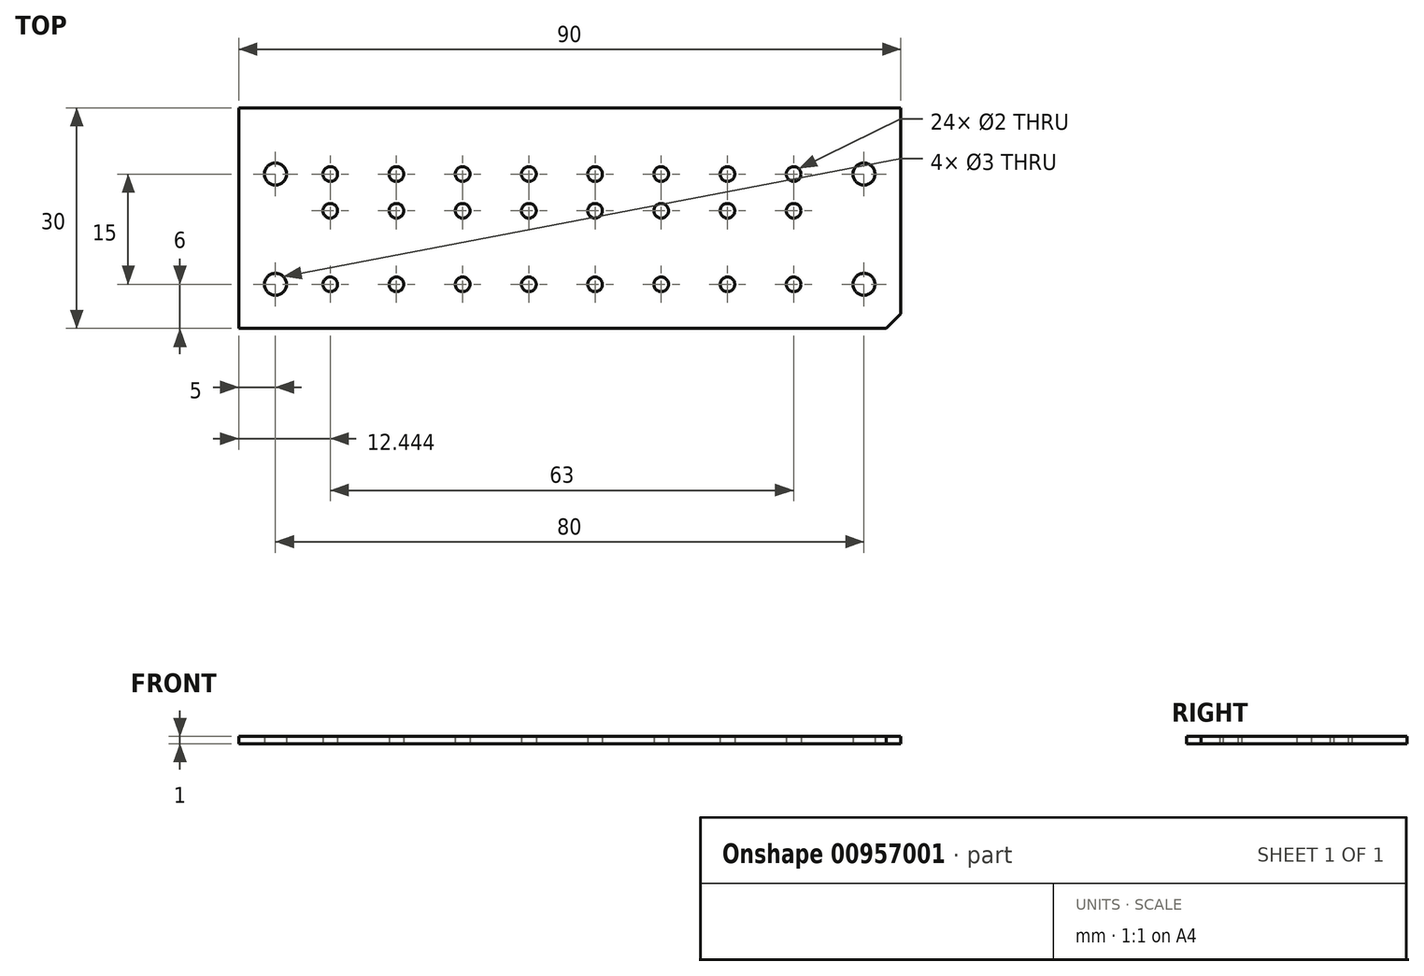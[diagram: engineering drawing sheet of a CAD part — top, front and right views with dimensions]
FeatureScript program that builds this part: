
annotation { "Feature Type Name" : "Feature", "Feature Type Description" : "" }
export const myFeature = defineFeature(function(context is Context, id is Id, definition is map)
    precondition{}
    {
        {
            var Q0;
            Q0=qCreatedBy(makeId("Top.planeOp"),FACE);
            var sketch = newSketch(context, id + "F0", { "sketchPlane" : qUnion([Q0])});
            skLineSegment(sketch, "E0.bottom", {"start": v(0, 0) * mm, "end": v(90, 0) * mm});
            skLineSegment(sketch, "E0.top", {"start": v(0, 30) * mm, "end": v(90, 30) * mm});
            skLineSegment(sketch, "E0.left", {"start": v(0, 0) * mm, "end": v(0, 30) * mm});
            skLineSegment(sketch, "E0.right", {"start": v(90, 0) * mm, "end": v(90, 30) * mm});
            skSolve(sketch);
        }
        {
            var Q0;
            Q0 = qSketchRegion(id + "F0", true);
            extrude(context, id + "F1", {"entities" : qUnion([Q0]), "depth" : 1 * mm, "offsetDistance" : 25 * mm});
        }
        {
            var Q0;
            Q0=qCreatedBy(makeId("Top.planeOp"),FACE);
            var sketch = newSketch(context, id + "F2", { "sketchPlane" : qUnion([Q0])});
            skCircle(sketch, "E1", {"center": v(12.44, 6) * mm, "radius": 1 * mm});
            skCircle(sketch, "E2", {"center": v(12.44, 21) * mm, "radius": 1 * mm});
            skCircle(sketch, "E3", {"center": v(12.44, 16) * mm, "radius": 1 * mm});
            skCircle(sketch, "E4.1.0.0", {"center": v(21.44, 21) * mm, "radius": 1 * mm});
            skCircle(sketch, "E4.1.0.1", {"center": v(21.44, 16) * mm, "radius": 1 * mm});
            skCircle(sketch, "E4.1.0.2", {"center": v(21.44, 6) * mm, "radius": 1 * mm});
            skCircle(sketch, "E4.2.0.0", {"center": v(30.44, 21) * mm, "radius": 1 * mm});
            skCircle(sketch, "E4.2.0.1", {"center": v(30.44, 16) * mm, "radius": 1 * mm});
            skCircle(sketch, "E4.2.0.2", {"center": v(30.44, 6) * mm, "radius": 1 * mm});
            skCircle(sketch, "E4.3.0.0", {"center": v(39.44, 21) * mm, "radius": 1 * mm});
            skCircle(sketch, "E4.3.0.1", {"center": v(39.44, 16) * mm, "radius": 1 * mm});
            skCircle(sketch, "E4.3.0.2", {"center": v(39.44, 6) * mm, "radius": 1 * mm});
            skCircle(sketch, "E4.4.0.0", {"center": v(48.44, 21) * mm, "radius": 1 * mm});
            skCircle(sketch, "E4.4.0.1", {"center": v(48.44, 16) * mm, "radius": 1 * mm});
            skCircle(sketch, "E4.4.0.2", {"center": v(48.44, 6) * mm, "radius": 1 * mm});
            skCircle(sketch, "E4.5.0.0", {"center": v(57.44, 21) * mm, "radius": 1 * mm});
            skCircle(sketch, "E4.5.0.1", {"center": v(57.44, 16) * mm, "radius": 1 * mm});
            skCircle(sketch, "E4.5.0.2", {"center": v(57.44, 6) * mm, "radius": 1 * mm});
            skCircle(sketch, "E4.6.0.0", {"center": v(66.44, 21) * mm, "radius": 1 * mm});
            skCircle(sketch, "E4.6.0.1", {"center": v(66.44, 16) * mm, "radius": 1 * mm});
            skCircle(sketch, "E4.6.0.2", {"center": v(66.44, 6) * mm, "radius": 1 * mm});
            skCircle(sketch, "E4.7.0.0", {"center": v(75.44, 21) * mm, "radius": 1 * mm});
            skCircle(sketch, "E4.7.0.1", {"center": v(75.44, 16) * mm, "radius": 1 * mm});
            skCircle(sketch, "E4.7.0.2", {"center": v(75.44, 6) * mm, "radius": 1 * mm});
            skLineSegment(sketch, "E4.direction1", {"start": v(12.44, 21) * mm, "end": v(21.44, 21) * mm, "construction": true});
            skSolve(sketch);
        }
        {
            var Q0;
            Q0 = qSketchRegion(id + "F2", true);
            var Q1;
            Q1=makeQuery(id+"F1.opExtrude","CAP_FACE",FACE,{"disambiguationData":[OSD([sQuery(id+"F0.wireOp",EDGE,"E0.bottom"),sQuery(id+"F0.wireOp",EDGE,"E0.top"),sQuery(id+"F0.wireOp",EDGE,"E0.left"),sQuery(id+"F0.wireOp",EDGE,"E0.right")])],"isStart":false});
            extrude(context, id + "F3", {"entities" : qUnion([Q0]), "operationType" : NewBodyOperationType.REMOVE, "endBound" : BoundingType.UP_TO_SURFACE, "depth" : 25 * mm, "endBoundEntityFace" : qUnion([Q1]), "offsetDistance" : 25 * mm});
        }
        {
            var Q0;
            Q0=makeQuery(id+"F1.opExtrude","SWEPT_EDGE",EDGE,{"disambiguationData":[OSD([sQuery(id+"F0.wireOp",EDGE,"E0.bottom"),sQuery(id+"F0.wireOp",EDGE,"E0.right")])]});
            chamfer(context, id + "F4", {"entities" : qUnion([Q0]), "width" : 2 * mm, "tangentPropagation" : true});
        }
        {
            var Q0;
            Q0=qCreatedBy(makeId("Top.planeOp"),FACE);
            var sketch = newSketch(context, id + "F5", { "sketchPlane" : qUnion([Q0])});
            skCircle(sketch, "E5", {"center": v(5, 6) * mm, "radius": 1.5 * mm});
            skCircle(sketch, "E6", {"center": v(5, 21) * mm, "radius": 1.5 * mm});
            skCircle(sketch, "E7.1.0.0", {"center": v(85, 21) * mm, "radius": 1.5 * mm});
            skCircle(sketch, "E7.1.0.1", {"center": v(85, 6) * mm, "radius": 1.5 * mm});
            skLineSegment(sketch, "E7.direction1", {"start": v(5, 21) * mm, "end": v(85, 21) * mm, "construction": true});
            skSolve(sketch);
        }
        {
            var Q0;
            Q0 = qSketchRegion(id + "F5", true);
            var Q1;
            Q1=makeQuery(id+"F1.opExtrude","CAP_FACE",FACE,{"disambiguationData":[OSD([sQuery(id+"F0.wireOp",EDGE,"E0.bottom"),sQuery(id+"F0.wireOp",EDGE,"E0.top"),sQuery(id+"F0.wireOp",EDGE,"E0.left"),sQuery(id+"F0.wireOp",EDGE,"E0.right")])],"isStart":false});
            extrude(context, id + "F6", {"entities" : qUnion([Q0]), "operationType" : NewBodyOperationType.REMOVE, "endBound" : BoundingType.UP_TO_SURFACE, "depth" : 25 * mm, "endBoundEntityFace" : qUnion([Q1]), "offsetDistance" : 25 * mm});
        }
    });
